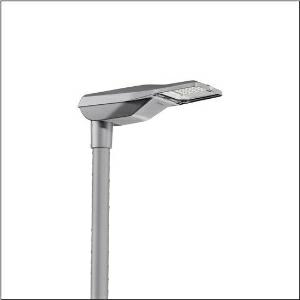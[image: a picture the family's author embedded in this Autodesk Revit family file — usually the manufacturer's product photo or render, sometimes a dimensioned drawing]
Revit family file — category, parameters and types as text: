
# Revit family: streetlight_sl_21_iq_micro___p0_8a_5xe1u31g08db_89ec
name_source: partatom
category: Lighting Fixtures
units: mm (PartAtom-declared; Revit-internal decimal feet)

## family parameters
Cut with Voids When Loaded = No
Host = Face
Light Source = No
Part Type = Normal
Room Calculation Point = No
Round Connector Dimension = Use Diameter
Shared = No

## types (1)
- --- (1 x LED, 4750 lm, 36.4 W, 3000K)
    Apparent Load = 36 VA
    CIE Flux Codes = 33 69 96 100 100
    Color Rendering = 70
    Color Temperature = 3000K
    Default Elevation = 1800 mm
    Description = Streetlight SL 21 iQ micro, mast luminaire, primary light control with lens, of PMMA, primary optical cover: cover, of toughened safety glass, transparent, light distribution: P0.8a, light emission: direct distribution, primary light characteristic: asymmetric, installation type: post-top, side-entry, LED, High Power LED, rated luminous flux: 4.750lm, luminous efficacy: 131lm/W, light colour: 730, colour temperature: 3000K, control gear: iQ Street-Remote, control: pre-setting: linear dimming characteristic, Street-Remote, Auto-Match, Temp-Guard, Lumen-Switch, Night-Set, Smart-Wire, Light-Fading, Desk-Remote (wireless, voltage-free reading and setting of iQ features in the workshop via application-optimized NFC function/RFID function), optimised constant luminous flux control (CLO 2.0), mains connection: 220..240V, AC, 50/60Hz, start of lifetime: 36W, end of service life: 38W, reduction: 16W, luminaire housing, of diecast aluminium, powder-coated, Siteco® metallic grey (DB 702S), corrosivity category C5 mid according to DIN EN ISO 12944, please order mast flange separately, inclination adjustable: 0°, 5°, 10°, 15°, sealing non-destructively replaceable, multi-level sealing system, length: 528mm, width: 235mm, height: 110mm, mast flange for spigot size: 42mm (side-entry): 5XC10008XM4, 60/48mm (side-entry/post-top): 5XC10108XM2, 76/60mm (side-entry/post-top): 5XC10108XM1, protection rating (complete): IP66, insulation class (complete): insulation class II (safety insulation), certification: CE, ENEC, ENEC+, VDE, impact resistance: IK10, permissible operating ambient temperature for outdoor applications: -40..+50°C, standard-compliant lighting for roads and squares, packaging unit: 1 piece

Light Distribution: P0.8a
    Height = 110 mm
    Lamp = 1 x LED
    Lamp Light Flux = 4750 lm
    Lamp Power = 36.4 W
    Lamp count = 1
    Length = 528 mm
    Luminous efficacy = 130 lm/W
    Manufacturer = Siteco
    ModVariant = No
    Model = 5XE1U31G08DB
    Number of Poles = 1
    OnlyDefault = Yes
    Power Factor = 1
    Product Name = Streetlight SL 21 iQ micro | P0.8a
    Product group = mast luminaire | pylon top
    ProductGroupID = 6100
    Protection Class = Protection class II
    Protection Degree = IP 66
    RLX_Detail_Level = 1
    RLX_Emergency_Light_Flux = 0 lm
    RLX_Emergency_Type = 0
    RLX_Emergency_Type_DB = No
    RlxData = <blob elided: 98909 chars, md5=6a68c544>
    Socket = socket
    Standby Power = 0 W
    System Light Flux = 4750 lm
    System Power = 36 W
    Type Comments = factory setting: luminous flux: 100 % | dim-lin: 254 | 715 mA
    Type Image = l_1006881.jpg
    URL = http://relux.com
    VarID = @adj_073076
    Voltage = 0 V
    Weight = 0.00 kg
    Width = 235 mm

## geometry (parser evidence)
native form markers: Blend x4, Sweep x11
no freeform markers — native parametric forms only
